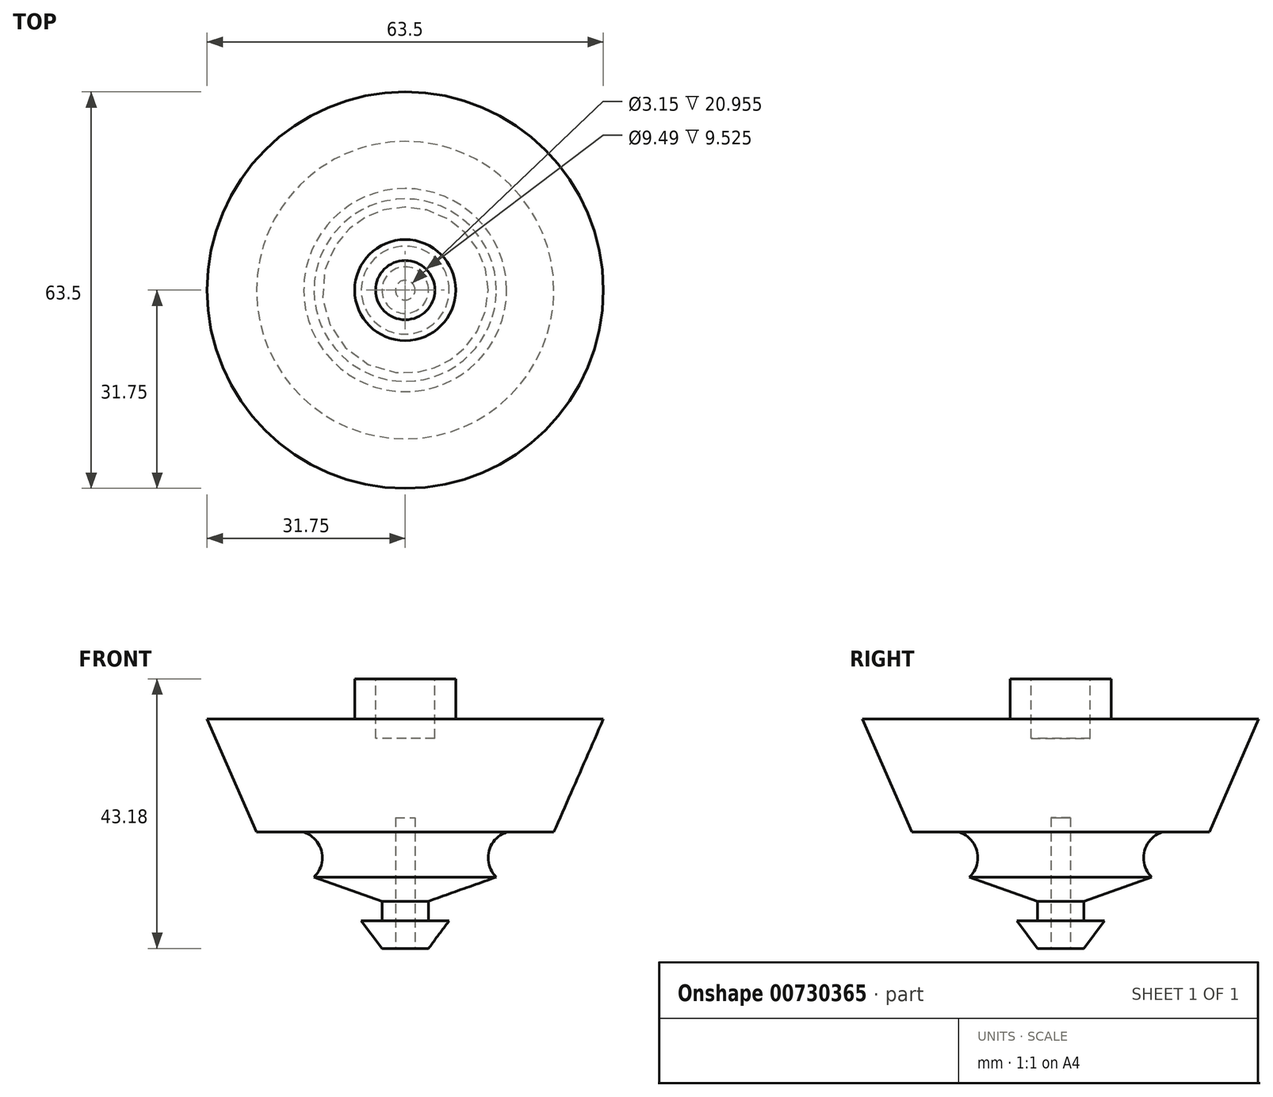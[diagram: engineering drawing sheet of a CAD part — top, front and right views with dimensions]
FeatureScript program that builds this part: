
annotation { "Feature Type Name" : "Feature", "Feature Type Description" : "" }
export const myFeature = defineFeature(function(context is Context, id is Id, definition is map)
    precondition{}
    {
        {
            var Q0;
            Q0=qCreatedBy(makeId("Front.planeOp"),FACE);
            var sketch = newSketch(context, id + "F0", { "sketchPlane" : qUnion([Q0])});
            skLineSegment(sketch, "E0.right", {"start": v(0, 6.73) * mm, "end": v(0, 20.97) * mm});
            skLineSegment(sketch, "E1", {"start": v(0, 6.73) * mm, "end": v(0, -22.21) * mm});
            skLineSegment(sketch, "E2", {"start": v(0, 20.97) * mm, "end": v(8.1, 20.97) * mm});
            skLineSegment(sketch, "E3", {"start": v(0, -22.21) * mm, "end": v(3.73, -22.21) * mm});
            skLineSegment(sketch, "E4", {"start": v(8.1, 20.97) * mm, "end": v(8.1, 14.5) * mm});
            skLineSegment(sketch, "E5", {"start": v(8.1, 14.5) * mm, "end": v(14.6, 14.5) * mm});
            skLineSegment(sketch, "E6", {"start": v(3.73, -22.21) * mm, "end": v(7.05, -17.8) * mm});
            skLineSegment(sketch, "E7", {"start": v(7.05, -17.8) * mm, "end": v(3.73, -17.8) * mm});
            skLineSegment(sketch, "E8", {"start": v(3.73, -17.8) * mm, "end": v(3.73, -14.66) * mm});
            skLineSegment(sketch, "E9", {"start": v(3.73, -14.66) * mm, "end": v(14.6, -10.78) * mm});
            skArc(sketch, "E10", {"start": v(16.26, -3.6) * mm, "mid": v(13.4, -6.72) * mm, "end": v(14.6, -10.78) * mm});
            skLineSegment(sketch, "E11", {"start": v(16.26, -3.6) * mm, "end": v(23.82, -3.6) * mm});
            skLineSegment(sketch, "E12", {"start": v(23.82, -3.6) * mm, "end": v(31.75, 14.5) * mm});
            skLineSegment(sketch, "E13", {"start": v(14.6, 14.5) * mm, "end": v(31.75, 14.5) * mm});
            skSolve(sketch);
        }
        {
            var Q0;
            Q0=makeQuery(id+"F0.imprint","IMPRINT",FACE,{"disambiguationData":[TD([[makeQuery(id+"F0.imprint","IMPRINT",EDGE,{"derivedFrom":sQuery(id+"F0.wireOp",EDGE,"iLR1ypYi-D9K4-WUiZ-luBJ-prHopcUQMVtk")}),1.0]])]});
            var Q1;
            Q1=makeQuery(id+"F0.imprint","IMPRINT",FACE,{"disambiguationData":[TD([[makeQuery(id+"F0.imprint","IMPRINT",EDGE,{"derivedFrom":sQuery(id+"F0.wireOp",EDGE,"E0.right")}),-1.0]])]});
            var Q2;
            Q2=sQuery(id+"F0.wireOp",EDGE,"E1");
            revolve(context, id + "F1", {"surfaceOperationType" : NewSurfaceOperationType.NEW, "entities" : qUnion([Q0, Q1]), "axis" : qUnion([Q2]), "revolveType" : RevolveType.FULL});
        }
        {
            var Q0;
            Q0=makeQuery(id+"F1.opRevolve","SWEPT_FACE",FACE,{"disambiguationData":[OSD([sQuery(id+"F0.wireOp",EDGE,"E3")])]});
            var sketch = newSketch(context, id + "F2", { "sketchPlane" : qUnion([Q0])});
            skCircle(sketch, "E14", {"center": v(0, 0) * mm, "radius": 1.57 * mm});
            skSolve(sketch);
        }
        {
            var Q0;
            Q0=makeQuery(id+"F2.imprint","IMPRINT",FACE,{"disambiguationData":[TD([[makeQuery(id+"F2.imprint","IMPRINT",EDGE,{"derivedFrom":sQuery(id+"F2.wireOp",EDGE,"E14")}),1.0]])]});
            extrude(context, id + "F3", {"entities" : qUnion([Q0]), "operationType" : NewBodyOperationType.REMOVE, "oppositeDirection" : true, "depth" : 20.95 * mm, "offsetDistance" : 25.4 * mm});
        }
        {
            var Q0;
            Q0=makeQuery(id+"F1.opRevolve","SWEPT_FACE",FACE,{"disambiguationData":[OSD([sQuery(id+"F0.wireOp",EDGE,"E2")])]});
            var sketch = newSketch(context, id + "F4", { "sketchPlane" : qUnion([Q0])});
            skCircle(sketch, "E15", {"center": v(0, 0) * mm, "radius": 4.75 * mm});
            skSolve(sketch);
        }
        {
            var Q0;
            Q0=makeQuery(id+"F4.imprint","IMPRINT",FACE,{"disambiguationData":[TD([[makeQuery(id+"F4.imprint","IMPRINT",EDGE,{"derivedFrom":sQuery(id+"F4.wireOp",EDGE,"E15")}),1.0]])]});
            extrude(context, id + "F5", {"entities" : qUnion([Q0]), "operationType" : NewBodyOperationType.REMOVE, "oppositeDirection" : true, "depth" : 9.52 * mm, "offsetDistance" : 25.4 * mm});
        }
    });
